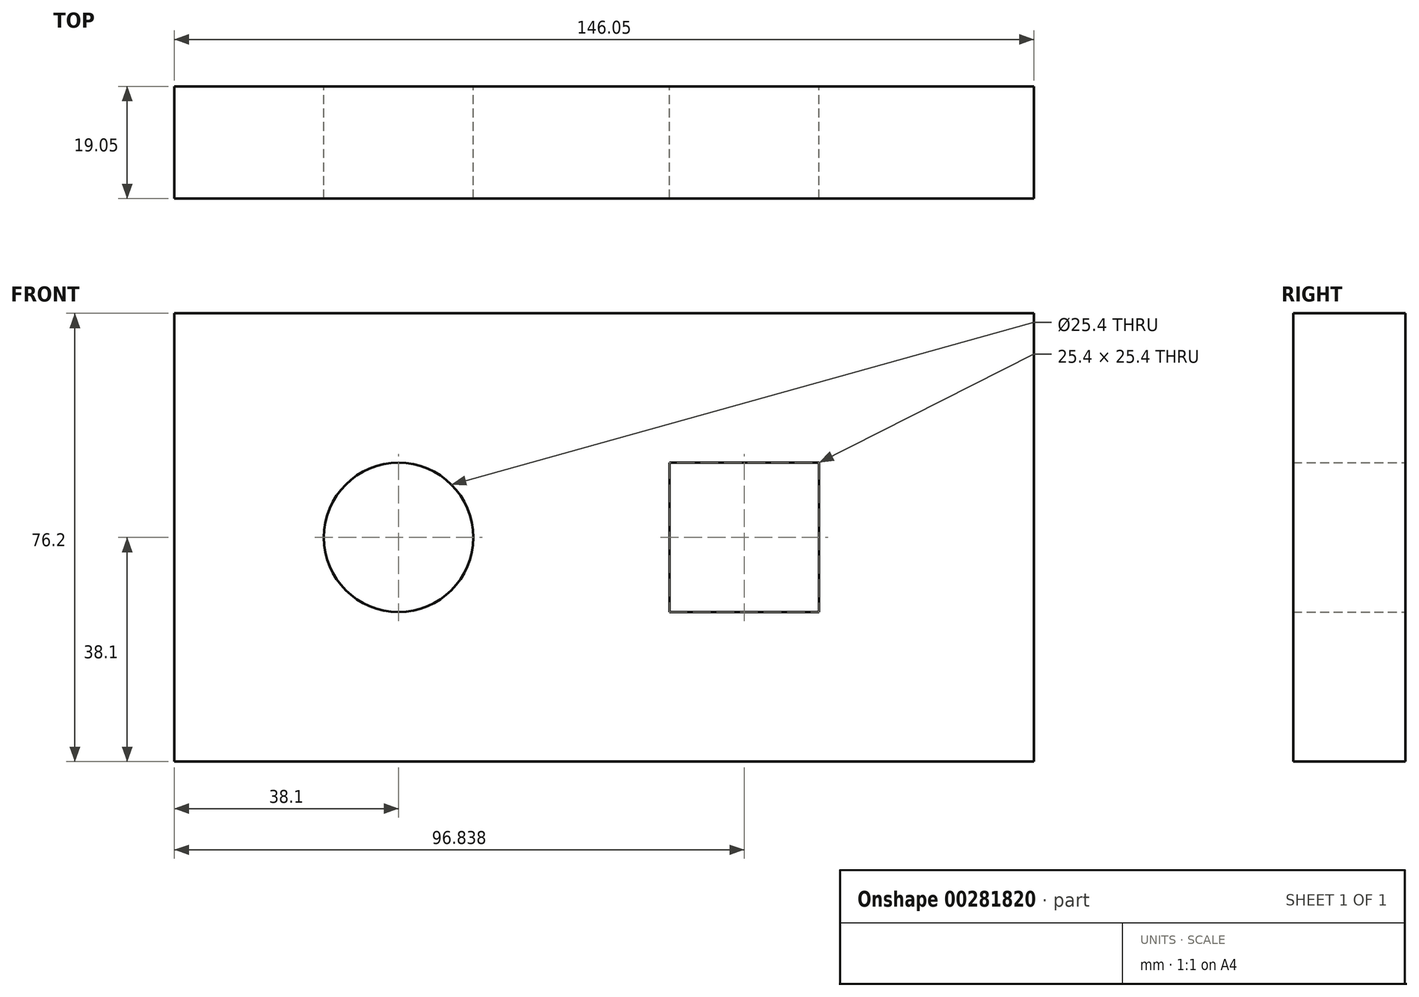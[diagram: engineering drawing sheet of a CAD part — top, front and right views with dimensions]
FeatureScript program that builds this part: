
annotation { "Feature Type Name" : "Feature", "Feature Type Description" : "" }
export const myFeature = defineFeature(function(context is Context, id is Id, definition is map)
    precondition{}
    {
        {
            var Q0;
            Q0=qCreatedBy(makeId("Front.planeOp"),FACE);
            var sketch = newSketch(context, id + "F0", { "sketchPlane" : qUnion([Q0])});
            skLineSegment(sketch, "E0.bottom", {"start": v(0, 0) * mm, "end": v(-146.05, 0) * mm});
            skLineSegment(sketch, "E0.top", {"start": v(0, 76.2) * mm, "end": v(-146.05, 76.2) * mm});
            skLineSegment(sketch, "E0.left", {"start": v(0, 0) * mm, "end": v(0, 76.2) * mm});
            skLineSegment(sketch, "E0.right", {"start": v(-146.05, 0) * mm, "end": v(-146.05, 76.2) * mm});
            skLineSegment(sketch, "E1.bottom", {"start": v(-36.51, 25.4) * mm, "end": v(-61.91, 25.4) * mm});
            skLineSegment(sketch, "E1.top", {"start": v(-36.51, 50.8) * mm, "end": v(-61.91, 50.8) * mm});
            skLineSegment(sketch, "E1.left", {"start": v(-36.51, 25.4) * mm, "end": v(-36.51, 50.8) * mm});
            skLineSegment(sketch, "E1.right", {"start": v(-61.91, 25.4) * mm, "end": v(-61.91, 50.8) * mm});
            skCircle(sketch, "E2", {"center": v(-107.95, 38.1) * mm, "radius": 12.7 * mm});
            skSolve(sketch);
        }
        {
            var Q0;
            Q0 = qSketchRegion(id + "F0", true);
            extrude(context, id + "F1", {"entities" : qUnion([Q0]), "depth" : 19.05 * mm});
        }
    });
